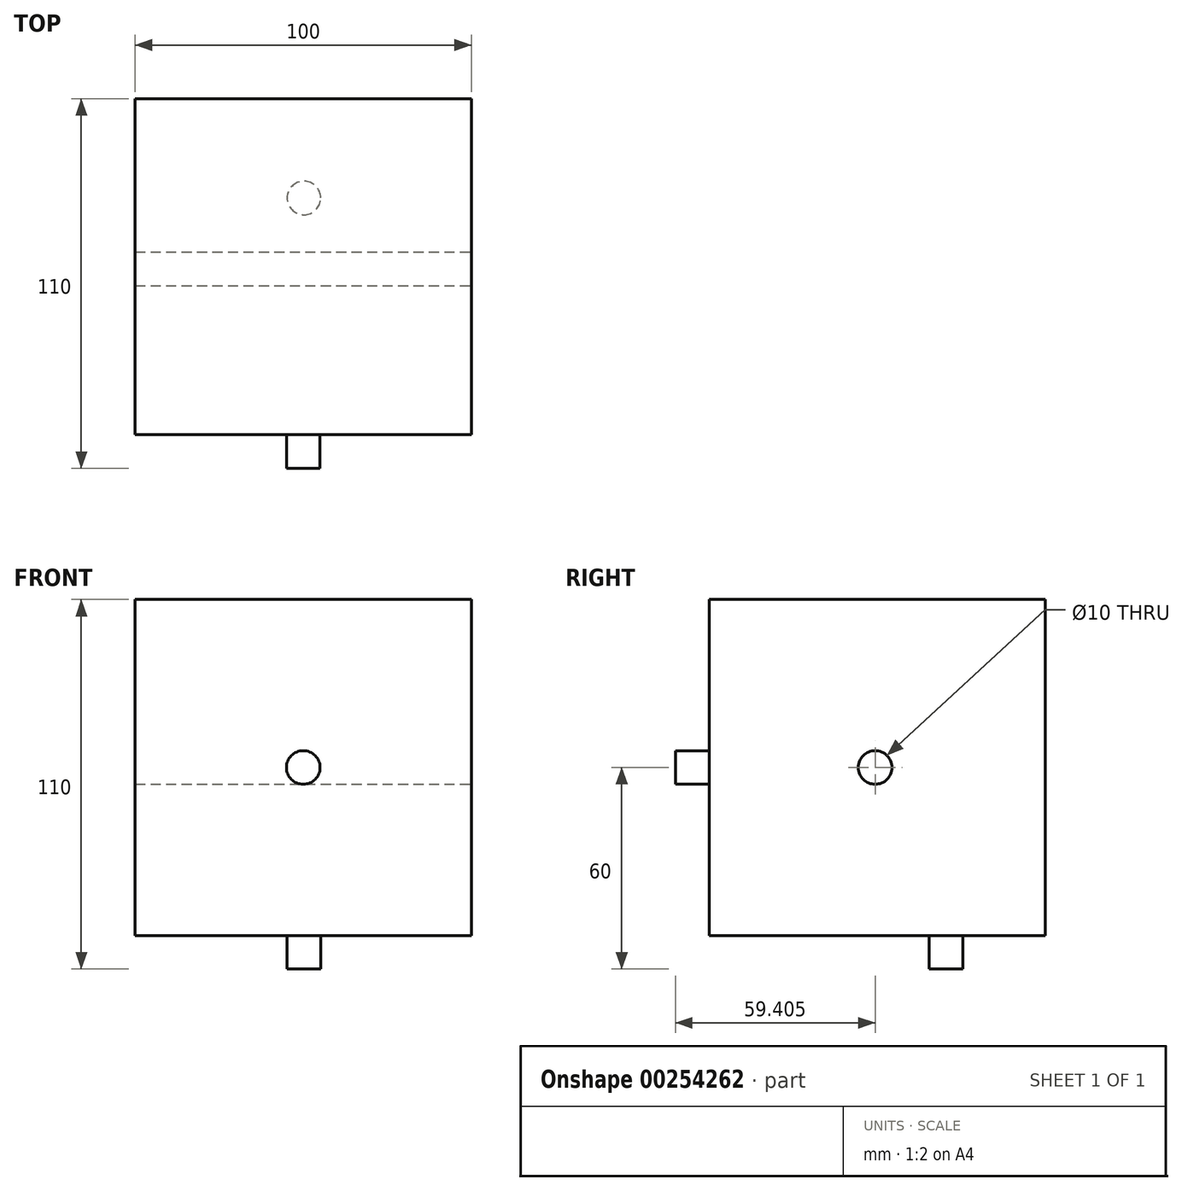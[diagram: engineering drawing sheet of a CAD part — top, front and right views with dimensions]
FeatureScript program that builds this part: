
annotation { "Feature Type Name" : "Feature", "Feature Type Description" : "" }
export const myFeature = defineFeature(function(context is Context, id is Id, definition is map)
    precondition{}
    {
        {
            var Q0;
            Q0=qCreatedBy(makeId("Front.planeOp"),FACE);
            var sketch = newSketch(context, id + "F0", { "sketchPlane" : qUnion([Q0])});
            skLineSegment(sketch, "E0.bottom", {"start": v(50, 50) * mm, "end": v(-50, 50) * mm});
            skLineSegment(sketch, "E0.top", {"start": v(50, -50) * mm, "end": v(-50, -50) * mm});
            skLineSegment(sketch, "E0.left", {"start": v(50, 50) * mm, "end": v(50, -50) * mm});
            skLineSegment(sketch, "E0.right", {"start": v(-50, 50) * mm, "end": v(-50, -50) * mm});
            skPoint(sketch, "E0.middle", {"position": v(0, 0) * mm});
            skSolve(sketch);
        }
        {
            var Q0;
            Q0 = qSketchRegion(id + "F0", true);
            extrude(context, id + "F1", {"entities" : qUnion([Q0]), "depth" : 100 * mm});
        }
        {
            var Q0;
            Q0=makeQuery(id+"F1.opExtrude","CAP_FACE",FACE,{"disambiguationData":[OSD([sQuery(id+"F0.wireOp",EDGE,"E0.bottom"),sQuery(id+"F0.wireOp",EDGE,"E0.top"),sQuery(id+"F0.wireOp",EDGE,"E0.left"),sQuery(id+"F0.wireOp",EDGE,"E0.right")])],"isStart":false});
            var sketch = newSketch(context, id + "F2", { "sketchPlane" : qUnion([Q0])});
            skCircle(sketch, "E1", {"center": v(0, 0) * mm, "radius": 5 * mm});
            skSolve(sketch);
        }
        {
            var Q0;
            Q0 = qSketchRegion(id + "F2", true);
            extrude(context, id + "F3", {"entities" : qUnion([Q0]), "operationType" : NewBodyOperationType.ADD, "depth" : 10 * mm});
        }
        {
            var Q0;
            Q0=makeQuery(id+"F1.opExtrude","SWEPT_FACE",FACE,{"disambiguationData":[OSD([sQuery(id+"F0.wireOp",EDGE,"E0.top")])]});
            var sketch = newSketch(context, id + "F4", { "sketchPlane" : qUnion([Q0])});
            skCircle(sketch, "E2", {"center": v(0.2, 29.51) * mm, "radius": 5 * mm});
            skPoint(sketch, "E2.first.point", {"position": v(0, 34.5) * mm});
            skPoint(sketch, "E2.second.point", {"position": v(0, 24.51) * mm});
            skPoint(sketch, "E2.third.point", {"position": v(5.12, 28.63) * mm});
            skSolve(sketch);
        }
        {
            var Q0;
            Q0=makeQuery(id+"F4.imprint","IMPRINT",FACE,{"disambiguationData":[TD([[makeQuery(id+"F4.imprint","IMPRINT",EDGE,{"derivedFrom":sQuery(id+"F4.wireOp",EDGE,"E2")}),1.0]])]});
            extrude(context, id + "F5", {"entities" : qUnion([Q0]), "operationType" : NewBodyOperationType.ADD, "depth" : 10 * mm});
        }
        {
            var Q0;
            Q0=makeQuery(id+"F1.opExtrude","SWEPT_FACE",FACE,{"disambiguationData":[OSD([sQuery(id+"F0.wireOp",EDGE,"E0.left")])]});
            var sketch = newSketch(context, id + "F6", { "sketchPlane" : qUnion([Q0])});
            skPoint(sketch, "E3", {"position": v(-50.6, 0) * mm});
            skSolve(sketch);
        }
        {
            var Q0;
            Q0=sQuery(id+"F6.wireOp",VERTEX,"E3");
            var Q1;
            Q1=makeQuery(id+"F1.opExtrude","SWEPT_BODY",BODY,{"disambiguationData":[OSD([sQuery(id+"F0.wireOp",EDGE,"E0.bottom"),sQuery(id+"F0.wireOp",EDGE,"E0.top"),sQuery(id+"F0.wireOp",EDGE,"E0.left"),sQuery(id+"F0.wireOp",EDGE,"E0.right")])]});
            hole(context, id + "F7", {"style" : HoleStyle.SIMPLE, "endStyle" : HoleEndStyle.THROUGH, "holeDiameter" : 10 * mm, "tappedDepth" : 12 * mm, "tapClearance" : 3, "locations" : qUnion([Q0]), "scope" : qUnion([Q1])});
        }
    });
